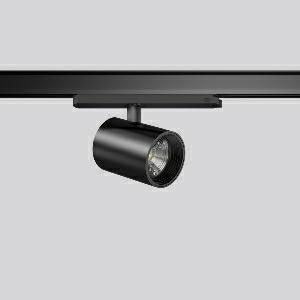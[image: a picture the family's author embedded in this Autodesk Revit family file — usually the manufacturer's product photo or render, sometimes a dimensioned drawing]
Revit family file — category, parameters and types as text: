
# Revit family: deecos_s_mini_track-in_742262_003_2_cecd
name_source: partatom
category: Lighting Fixtures
units: mm (PartAtom-declared; Revit-internal decimal feet)

## family parameters
Cut with Voids When Loaded = No
Host = Face
Light Source = No
Part Type = Normal
Room Calculation Point = No
Round Connector Dimension = Use Diameter
Shared = No

## types (1)
- DEECOS S mini track-in (1 x LED Modul 927, 2850 lm, 2700)
    Apparent Load = 29 VA
    Approval mark = CE
    CIE Flux Codes = 96 100 100 100 100
    Color Rendering = 92
    Color Temperature = 2700
    Default Elevation = 1800 mm
    Description = Series: DEECOS S mini track-in
LED surface-mounted projector in modern design with no visible cooling ribs. Housing: die-cast aluminium, powder-coated. Rotation range: 356°. Swivel range: 90°. Black plastic ring and recessed LED to prevent glare from the side. Optical assembly with lens made of plastic (polycarbonate) for the best homogeneous light distribution - can be changed without tools. Best colour rendering index Ra>90. With multi adaptor for 3-circuit tracks 230 V. Suitable for Track on ceiling, Wall track. Track-in driver integrated into the adapter. High quality converter without flickering and stroboscopic effect. The following accessories can be mounted without use of tools: interchangeable lenses, decorative glasses, honeycomb louvre, clear and frosted diffusers, white interchangeable plastic ring. 
Colour: deep black, matt (RAL 9005)
Diameter: 87 mm
Height: 135 mm
Lamp: LED
Socket: without socket
Colour temperature: 2700K
Colour rendering index (CRI): 92
System power: 29 W
Rated luminous flux: 2850 lm
Luminous efficiency: 98 lm/W
Control gear: Regulated power supply
Protection class: II
Type of protection: IP 20
    Height = 135 mm
    Lamp = 1 x LED Modul 927
    Lamp Light Flux = 2850 lm
    Lamp count = 1
    Length = 87 mm
    Lifetime = 50000 h
    Luminous efficacy = 98 lm/W
    Manufacturer = RZB
    ModVariant = No
    Model = 742262.003.2
    Mounting Place = Ceiling
    Mounting Type = Rail mounted
    Number of Poles = 1
    OnlyDefault = Yes
    Power Factor = 1
    Product Name = DEECOS S mini track-in
    Product group = Track mounted projectors
    ProductGroupID = 301
    Protection Class = Protection class II
    Protection Degree = IP 20
    RLX_Detail_Level = 1
    RLX_Emergency_Light_Flux = 0 lm
    RLX_Emergency_Type = 0
    RLX_Emergency_Type_DB = No
    RlxData = <blob elided: 37441 chars, md5=637504be>
    Socket = socket
    Standby Power = 0 W
    System Light Flux = 2850 lm
    System Power = 29 W
    Type Comments = Product without accessories
    Type Image = 742108.003.jpg
    URL = http://relux.com
    VarID = ---
    Voltage = 230 V
    Voltage Range = 220-240 V
    Weight = 0.00 kg
    Width = 0 mm  [stored 0 ft]

note: [stored X ft] marks values corroborated as IEEE doubles in the binary element streams (Revit-internal decimal feet)

## geometry (parser evidence)
native form markers: Blend x4, Sweep x11
no freeform markers — native parametric forms only
